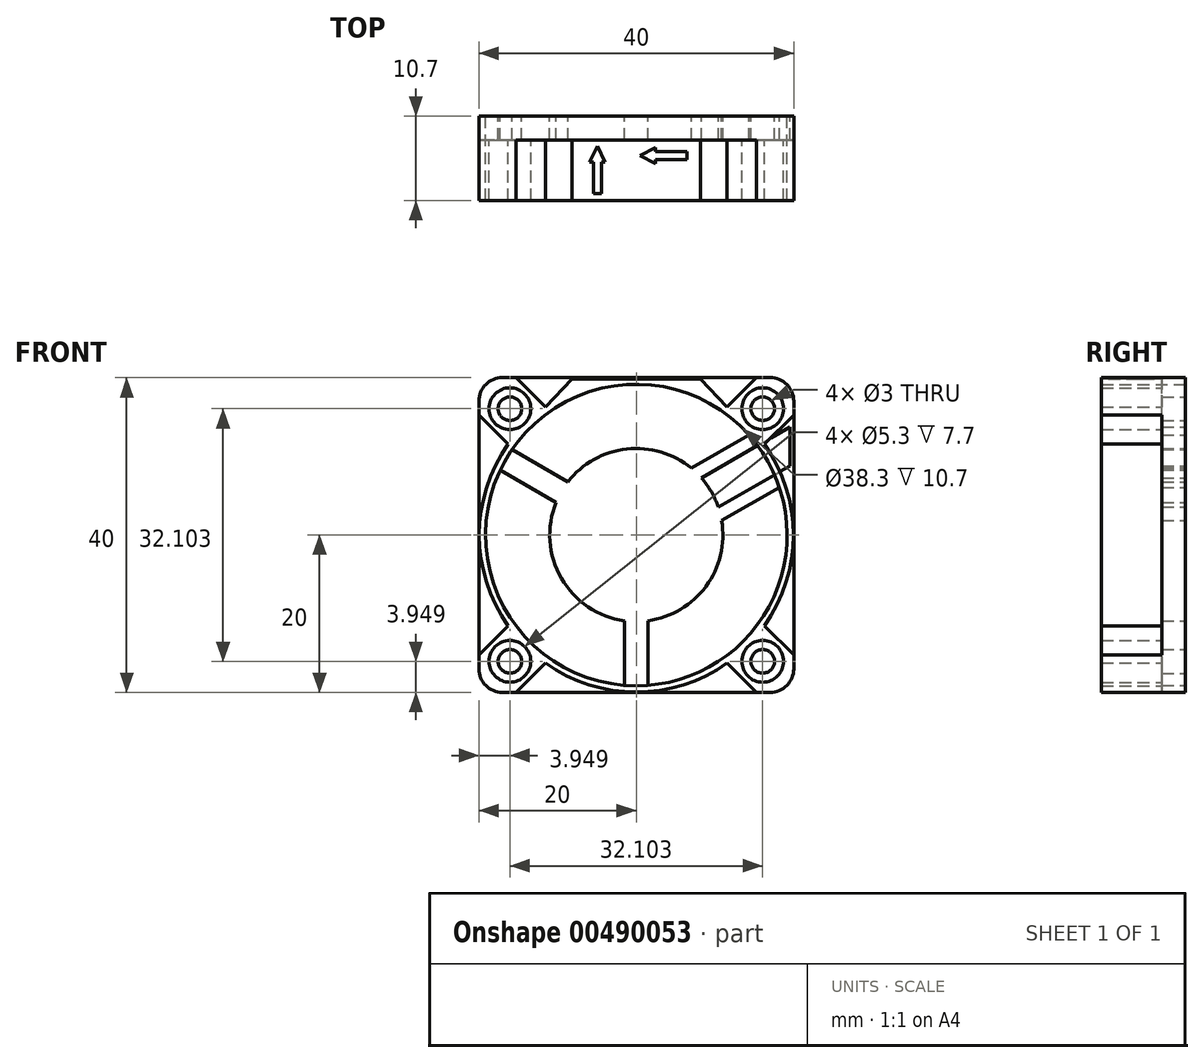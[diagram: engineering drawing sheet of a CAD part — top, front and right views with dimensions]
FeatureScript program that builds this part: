
annotation { "Feature Type Name" : "Feature", "Feature Type Description" : "" }
export const myFeature = defineFeature(function(context is Context, id is Id, definition is map)
    precondition{}
    {
        {
            var Q0;
            Q0=qCreatedBy(makeId("Front.planeOp"),FACE);
            var sketch = newSketch(context, id + "F0", { "sketchPlane" : qUnion([Q0])});
            skLineSegment(sketch, "E0.bottom", {"start": v(20, 20) * mm, "end": v(-20, 20) * mm});
            skLineSegment(sketch, "E0.top", {"start": v(20, -20) * mm, "end": v(-20, -20) * mm});
            skLineSegment(sketch, "E0.left", {"start": v(20, 20) * mm, "end": v(20, -20) * mm});
            skLineSegment(sketch, "E0.right", {"start": v(-20, 20) * mm, "end": v(-20, -20) * mm});
            skPoint(sketch, "E0.middle", {"position": v(0, 0) * mm});
            skCircle(sketch, "E1", {"center": v(0, 0) * mm, "radius": 19.15 * mm});
            skCircle(sketch, "E2", {"center": v(-16.05, 16.05) * mm, "radius": 2.65 * mm});
            skLineSegment(sketch, "E3", {"start": v(-20, 20) * mm, "end": v(0, 0) * mm, "construction": true});
            skLineSegment(sketch, "E4", {"start": v(-16.28, 11.54) * mm, "end": v(-20, 15.26) * mm});
            skCircle(sketch, "E5.0", {"center": v(0, 0) * mm, "radius": 19.95 * mm});
            skPoint(sketch, "E6", {"position": v(0, 25.11) * mm});
            skLineSegment(sketch, "E7.MirrorCS", {"start": v(-11.54, 16.28) * mm, "end": v(-15.26, 20) * mm});
            skLineSegment(sketch, "E8", {"start": v(-7.95, 20) * mm, "end": v(-11.54, 16.28) * mm});
            skCircle(sketch, "E9", {"center": v(-16.05, 16.05) * mm, "radius": 1.5 * mm});
            skLineSegment(sketch, "E10.1.0", {"start": v(-16.28, -11.54) * mm, "end": v(-20, -15.26) * mm});
            skCircle(sketch, "E10.1.1", {"center": v(-16.05, -16.05) * mm, "radius": 2.65 * mm});
            skCircle(sketch, "E10.1.2", {"center": v(-16.05, -16.05) * mm, "radius": 1.5 * mm});
            skLineSegment(sketch, "E10.1.3", {"start": v(-11.54, -16.28) * mm, "end": v(-15.26, -20) * mm});
            skLineSegment(sketch, "E10.2.0", {"start": v(11.54, -16.28) * mm, "end": v(15.26, -20) * mm});
            skCircle(sketch, "E10.2.1", {"center": v(16.05, -16.05) * mm, "radius": 2.65 * mm});
            skCircle(sketch, "E10.2.2", {"center": v(16.05, -16.05) * mm, "radius": 1.5 * mm});
            skLineSegment(sketch, "E10.2.3", {"start": v(16.28, -11.54) * mm, "end": v(20, -15.26) * mm});
            skLineSegment(sketch, "E10.3.0", {"start": v(16.28, 11.54) * mm, "end": v(20, 15.26) * mm});
            skCircle(sketch, "E10.3.1", {"center": v(16.05, 16.05) * mm, "radius": 2.65 * mm});
            skCircle(sketch, "E10.3.2", {"center": v(16.05, 16.05) * mm, "radius": 1.5 * mm});
            skLineSegment(sketch, "E10.3.3", {"start": v(11.54, 16.28) * mm, "end": v(15.26, 20) * mm});
            skLineSegment(sketch, "E11.MirrorCS", {"start": v(7.95, 20) * mm, "end": v(11.54, 16.28) * mm});
            skCircle(sketch, "E12", {"center": v(0, 0) * mm, "radius": 11 * mm});
            skLineSegment(sketch, "E13", {"start": v(-1.5, -10.9) * mm, "end": v(-1.5, -19.1) * mm});
            skLineSegment(sketch, "E14.MirrorCS", {"start": v(1.5, -10.9) * mm, "end": v(1.5, -19.1) * mm});
            skLineSegment(sketch, "E15.1.0", {"start": v(10.19, 4.15) * mm, "end": v(17.28, 8.25) * mm});
            skLineSegment(sketch, "E15.1.1", {"start": v(8.69, 6.75) * mm, "end": v(15.78, 10.84) * mm});
            skLineSegment(sketch, "E15.2.0", {"start": v(-8.69, 6.75) * mm, "end": v(-15.78, 10.84) * mm});
            skLineSegment(sketch, "E15.2.1", {"start": v(-10.19, 4.15) * mm, "end": v(-17.28, 8.25) * mm});
            skLineSegment(sketch, "E16", {"start": v(14.32, 12.71) * mm, "end": v(7, 8.49) * mm});
            skLineSegment(sketch, "E17", {"start": v(10.85, 1.82) * mm, "end": v(18.17, 6.05) * mm});
            skLineSegment(sketch, "E18", {"start": v(8.27, 7.26) * mm, "end": v(20, 14.03) * mm});
            skLineSegment(sketch, "E19", {"start": v(10.42, 3.53) * mm, "end": v(20, 9.06) * mm});
            skLineSegment(sketch, "E20", {"start": v(19.5, 13.74) * mm, "end": v(19.5, 8.78) * mm});
            skPoint(sketch, "E21", {"position": v(19.5, 11.26) * mm});
            skLineSegment(sketch, "E22.bottom", {"start": v(20, 12.76) * mm, "end": v(19.5, 12.76) * mm});
            skLineSegment(sketch, "E22.top", {"start": v(20, 9.76) * mm, "end": v(19.5, 9.76) * mm});
            skLineSegment(sketch, "E22.left", {"start": v(20, 12.76) * mm, "end": v(20, 9.76) * mm});
            skLineSegment(sketch, "E22.right", {"start": v(19.5, 12.76) * mm, "end": v(19.5, 9.76) * mm});
            skPoint(sketch, "E22.middle", {"position": v(19.75, 11.26) * mm});
            skSolve(sketch);
        }
        {
            var Q0;
            {var subQ0=sQuery(id+"F0.wireOp",EDGE,"E4");Q0=makeQuery(id+"F0.imprint","IMPRINT",FACE,{"disambiguationData":[TD([[makeQuery(id+"F0.imprint","IMPRINT",EDGE,{"derivedFrom":subQ0}),1.0]])]});}
            var Q1;
            {var subQ4=sQuery(id+"F0.wireOp",EDGE,"E1");var subQ6=makeQuery(id+"F0.imprint","INTERSECT",VERTEX,{"derivedFrom":[subQ4,sQuery(id+"F0.wireOp",EDGE,"E17")]});Q1=makeQuery(id+"F0.imprint","IMPRINT",FACE,{"disambiguationData":[TD([[makeQuery(id+"F0.imprint","IMPRINT",EDGE,{"disambiguationData":[TD([[subQ6,-1.0]])],"derivedFrom":subQ4}),-1.0]])]});}
            var Q2;
            Q2=makeQuery(id+"F0.imprint","IMPRINT",FACE,{"disambiguationData":[TD([[makeQuery(id+"F0.imprint","IMPRINT",EDGE,{"derivedFrom":sQuery(id+"F0.wireOp",EDGE,"E2")}),-1.0]])]});
            var Q3;
            {var subQ0=sQuery(id+"F0.wireOp",EDGE,"E7.MirrorCS");Q3=makeQuery(id+"F0.imprint","IMPRINT",FACE,{"disambiguationData":[TD([[makeQuery(id+"F0.imprint","IMPRINT",EDGE,{"derivedFrom":subQ0}),-1.0]])]});}
            var Q4;
            {var subQ0=sQuery(id+"F0.wireOp",EDGE,"E8");Q4=makeQuery(id+"F0.imprint","IMPRINT",FACE,{"disambiguationData":[TD([[makeQuery(id+"F0.imprint","IMPRINT",EDGE,{"derivedFrom":subQ0}),1.0]])]});}
            var Q5;
            {var subQ0=sQuery(id+"F0.wireOp",EDGE,"E10.3.3");Q5=makeQuery(id+"F0.imprint","IMPRINT",FACE,{"disambiguationData":[TD([[makeQuery(id+"F0.imprint","IMPRINT",EDGE,{"derivedFrom":subQ0}),1.0]])]});}
            var Q6;
            Q6=makeQuery(id+"F0.imprint","IMPRINT",FACE,{"disambiguationData":[TD([[makeQuery(id+"F0.imprint","IMPRINT",EDGE,{"derivedFrom":sQuery(id+"F0.wireOp",EDGE,"E10.3.1")}),-1.0]])]});
            var Q7;
            Q7=makeQuery(id+"F0.imprint","IMPRINT",FACE,{"disambiguationData":[TD([[makeQuery(id+"F0.imprint","IMPRINT",EDGE,{"derivedFrom":sQuery(id+"F0.wireOp",EDGE,"E2")}),1.0]])]});
            var Q8;
            Q8=makeQuery(id+"F0.imprint","IMPRINT",FACE,{"disambiguationData":[TD([[makeQuery(id+"F0.imprint","IMPRINT",EDGE,{"derivedFrom":sQuery(id+"F0.wireOp",EDGE,"E10.3.1")}),1.0]])]});
            var Q9;
            {var subQ0=sQuery(id+"F0.wireOp",EDGE,"E15.2.0");Q9=makeQuery(id+"F0.imprint","IMPRINT",FACE,{"disambiguationData":[TD([[makeQuery(id+"F0.imprint","IMPRINT",EDGE,{"derivedFrom":subQ0}),1.0]])]});}
            var Q10;
            {var subQ0=sQuery(id+"F0.wireOp",EDGE,"E12");var subQ5=makeQuery(id+"F0.imprint","INTERSECT",VERTEX,{"derivedFrom":[subQ0,sQuery(id+"F0.wireOp",EDGE,"E17")]});Q10=makeQuery(id+"F0.imprint","IMPRINT",FACE,{"disambiguationData":[TD([[makeQuery(id+"F0.imprint","IMPRINT",EDGE,{"disambiguationData":[TD([[subQ5,-1.0]])],"derivedFrom":subQ0}),1.0]])]});}
            var Q11;
            {var subQ0=sQuery(id+"F0.wireOp",EDGE,"E16");Q11=makeQuery(id+"F0.imprint","IMPRINT",FACE,{"disambiguationData":[TD([[makeQuery(id+"F0.imprint","IMPRINT",EDGE,{"derivedFrom":subQ0}),1.0]])]});}
            var Q12;
            {var subQ0=sQuery(id+"F0.wireOp",EDGE,"E17");Q12=makeQuery(id+"F0.imprint","IMPRINT",FACE,{"disambiguationData":[TD([[makeQuery(id+"F0.imprint","IMPRINT",EDGE,{"derivedFrom":subQ0}),1.0]])]});}
            var Q13;
            {var subQ4=sQuery(id+"F0.wireOp",EDGE,"E10.2.3");Q13=makeQuery(id+"F0.imprint","IMPRINT",FACE,{"disambiguationData":[TD([[makeQuery(id+"F0.imprint","IMPRINT",EDGE,{"derivedFrom":subQ4}),1.0]])]});}
            var Q14;
            {var subQ0=sQuery(id+"F0.wireOp",EDGE,"E10.3.0");var subQ1=sQuery(id+"F0.wireOp",EDGE,"E0.left");var subQ2=makeQuery(id+"F0.imprint","INTERSECT",VERTEX,{"derivedFrom":[subQ1,subQ0]});Q14=makeQuery(id+"F0.imprint","IMPRINT",FACE,{"disambiguationData":[TD([[makeQuery(id+"F0.imprint","IMPRINT",EDGE,{"disambiguationData":[TD([[subQ2,-1.0]])],"derivedFrom":subQ1}),-1.0]])]});}
            var Q15;
            {var subQ5=sQuery(id+"F0.wireOp",EDGE,"E20");Q15=makeQuery(id+"F0.imprint","IMPRINT",FACE,{"disambiguationData":[TD([[makeQuery(id+"F0.imprint","IMPRINT",EDGE,{"derivedFrom":subQ5}),1.0]])]});}
            var Q16;
            {var subQ0=sQuery(id+"F0.wireOp",EDGE,"E10.3.0");var subQ1=sQuery(id+"F0.wireOp",EDGE,"E5.0");var subQ2=makeQuery(id+"F0.imprint","INTERSECT",VERTEX,{"derivedFrom":[subQ1,subQ0]});Q16=makeQuery(id+"F0.imprint","IMPRINT",FACE,{"disambiguationData":[TD([[makeQuery(id+"F0.imprint","IMPRINT",EDGE,{"disambiguationData":[TD([[subQ2,-1.0]])],"derivedFrom":subQ1}),-1.0]])]});}
            var Q17;
            {var subQ0=sQuery(id+"F0.wireOp",EDGE,"E10.2.0");Q17=makeQuery(id+"F0.imprint","IMPRINT",FACE,{"disambiguationData":[TD([[makeQuery(id+"F0.imprint","IMPRINT",EDGE,{"derivedFrom":subQ0}),1.0]])]});}
            var Q18;
            {var subQ0=sQuery(id+"F0.wireOp",EDGE,"E10.1.3");Q18=makeQuery(id+"F0.imprint","IMPRINT",FACE,{"disambiguationData":[TD([[makeQuery(id+"F0.imprint","IMPRINT",EDGE,{"derivedFrom":subQ0}),1.0]])]});}
            var Q19;
            {var subQ0=sQuery(id+"F0.wireOp",EDGE,"E10.1.0");Q19=makeQuery(id+"F0.imprint","IMPRINT",FACE,{"disambiguationData":[TD([[makeQuery(id+"F0.imprint","IMPRINT",EDGE,{"derivedFrom":subQ0}),1.0]])]});}
            var Q20;
            Q20=makeQuery(id+"F0.imprint","IMPRINT",FACE,{"disambiguationData":[TD([[makeQuery(id+"F0.imprint","IMPRINT",EDGE,{"derivedFrom":sQuery(id+"F0.wireOp",EDGE,"E10.1.1")}),1.0]])]});
            var Q21;
            Q21=makeQuery(id+"F0.imprint","IMPRINT",FACE,{"disambiguationData":[TD([[makeQuery(id+"F0.imprint","IMPRINT",EDGE,{"derivedFrom":sQuery(id+"F0.wireOp",EDGE,"E10.2.1")}),1.0]])]});
            var Q22;
            {var subQ0=sQuery(id+"F0.wireOp",EDGE,"E13");Q22=makeQuery(id+"F0.imprint","IMPRINT",FACE,{"disambiguationData":[TD([[makeQuery(id+"F0.imprint","IMPRINT",EDGE,{"derivedFrom":subQ0}),1.0]])]});}
            extrude(context, id + "F1", {"entities" : qUnion([Q0, Q1, Q2, Q3, Q4, Q5, Q6, Q7, Q8, Q9, Q10, Q11, Q12, Q13, Q14, Q15, Q16, Q17, Q18, Q19, Q20, Q21, Q22]), "depth" : 3 * mm});
        }
        {
            var Q0;
            Q0=makeQuery(id+"F0.imprint","IMPRINT",FACE,{"disambiguationData":[TD([[makeQuery(id+"F0.imprint","IMPRINT",EDGE,{"derivedFrom":sQuery(id+"F0.wireOp",EDGE,"E10.3.1")}),-1.0]])]});
            var Q1;
            {var subQ0=sQuery(id+"F0.wireOp",EDGE,"E8");Q1=makeQuery(id+"F0.imprint","IMPRINT",FACE,{"disambiguationData":[TD([[makeQuery(id+"F0.imprint","IMPRINT",EDGE,{"derivedFrom":subQ0}),1.0]])]});}
            var Q2;
            Q2=makeQuery(id+"F0.imprint","IMPRINT",FACE,{"disambiguationData":[TD([[makeQuery(id+"F0.imprint","IMPRINT",EDGE,{"derivedFrom":sQuery(id+"F0.wireOp",EDGE,"E2")}),-1.0]])]});
            var Q3;
            {var subQ4=sQuery(id+"F0.wireOp",EDGE,"E1");var subQ6=makeQuery(id+"F0.imprint","INTERSECT",VERTEX,{"derivedFrom":[subQ4,sQuery(id+"F0.wireOp",EDGE,"E17")]});Q3=makeQuery(id+"F0.imprint","IMPRINT",FACE,{"disambiguationData":[TD([[makeQuery(id+"F0.imprint","IMPRINT",EDGE,{"disambiguationData":[TD([[subQ6,-1.0]])],"derivedFrom":subQ4}),-1.0]])]});}
            var Q4;
            {var subQ0=sQuery(id+"F0.wireOp",EDGE,"E1");var subQ9=makeQuery(id+"F0.imprint","INTERSECT",VERTEX,{"derivedFrom":[subQ0,sQuery(id+"F0.wireOp",EDGE,"E15.1.0")]});Q4=makeQuery(id+"F0.imprint","IMPRINT",FACE,{"disambiguationData":[TD([[makeQuery(id+"F0.imprint","IMPRINT",EDGE,{"disambiguationData":[TD([[subQ9,1.0]])],"derivedFrom":subQ0}),-1.0]])]});}
            var Q5;
            {var subQ0=sQuery(id+"F0.wireOp",EDGE,"E10.2.0");Q5=makeQuery(id+"F0.imprint","IMPRINT",FACE,{"disambiguationData":[TD([[makeQuery(id+"F0.imprint","IMPRINT",EDGE,{"derivedFrom":subQ0}),1.0]])]});}
            var Q6;
            {var subQ0=sQuery(id+"F0.wireOp",EDGE,"E10.1.0");Q6=makeQuery(id+"F0.imprint","IMPRINT",FACE,{"disambiguationData":[TD([[makeQuery(id+"F0.imprint","IMPRINT",EDGE,{"derivedFrom":subQ0}),1.0]])]});}
            var Q7;
            {var subQ0=sQuery(id+"F0.wireOp",EDGE,"E10.3.0");var subQ1=sQuery(id+"F0.wireOp",EDGE,"E5.0");var subQ2=makeQuery(id+"F0.imprint","INTERSECT",VERTEX,{"derivedFrom":[subQ1,subQ0]});Q7=makeQuery(id+"F0.imprint","IMPRINT",FACE,{"disambiguationData":[TD([[makeQuery(id+"F0.imprint","IMPRINT",EDGE,{"disambiguationData":[TD([[subQ2,-1.0]])],"derivedFrom":subQ1}),-1.0]])]});}
            extrude(context, id + "F2", {"entities" : qUnion([Q0, Q1, Q2, Q3, Q4, Q5, Q6, Q7]), "operationType" : NewBodyOperationType.ADD, "depth" : 10.7 * mm});
        }
        {
            var Q0;
            {var subQ0=sQuery(id+"F0.wireOp",EDGE,"E1");var subQ9=makeQuery(id+"F0.imprint","INTERSECT",VERTEX,{"derivedFrom":[subQ0,sQuery(id+"F0.wireOp",EDGE,"E15.1.0")]});Q0=makeQuery(id+"F0.imprint","IMPRINT",FACE,{"disambiguationData":[TD([[makeQuery(id+"F0.imprint","IMPRINT",EDGE,{"disambiguationData":[TD([[subQ9,1.0]])],"derivedFrom":subQ0}),-1.0]])]});}
            var Q1;
            {var subQ0=sQuery(id+"F0.wireOp",EDGE,"E10.3.0");var subQ1=sQuery(id+"F0.wireOp",EDGE,"E5.0");var subQ2=makeQuery(id+"F0.imprint","INTERSECT",VERTEX,{"derivedFrom":[subQ1,subQ0]});Q1=makeQuery(id+"F0.imprint","IMPRINT",FACE,{"disambiguationData":[TD([[makeQuery(id+"F0.imprint","IMPRINT",EDGE,{"disambiguationData":[TD([[subQ2,-1.0]])],"derivedFrom":subQ1}),-1.0]])]});}
            var Q2;
            {var subQ0=sQuery(id+"F0.wireOp",EDGE,"E15.2.0");var subQ1=sQuery(id+"F0.wireOp",EDGE,"E14.MirrorCS");var subQ2=sQuery(id+"F0.wireOp",EDGE,"E1");var subQ3=sQuery(id+"F0.wireOp",EDGE,"E12");var subQ4=sQuery(id+"F0.wireOp",EDGE,"E16");var subQ5=sQuery(id+"F0.wireOp",EDGE,"E13");var subQ6=sQuery(id+"F0.wireOp",EDGE,"E15.2.1");var subQ7=sQuery(id+"F0.wireOp",EDGE,"E17");var subQ8=makeQuery(id+"F0.imprint","INTERSECT",VERTEX,{"derivedFrom":[subQ3,sQuery(id+"F0.wireOp",EDGE,"E15.1.1")]});var subQ9=sQuery(id+"F0.wireOp",EDGE,"E18");var subQ10=makeQuery(id+"F0.imprint","INTERSECT",VERTEX,{"derivedFrom":[subQ3,subQ9]});var subQ11=makeQuery(id+"F0.imprint","INTERSECT",VERTEX,{"derivedFrom":[subQ3,sQuery(id+"F0.wireOp",EDGE,"E15.1.0")]});var subQ12=sQuery(id+"F0.wireOp",EDGE,"E19");var subQ13=makeQuery(id+"F0.imprint","INTERSECT",VERTEX,{"derivedFrom":[subQ2,subQ9]});var subQ14=sQuery(id+"F0.wireOp",EDGE,"E5.0");Q2=makeQuery(id+"F2.boolean.opBoolean","SPLIT",FACE,{"disambiguationData":[TD([makeQuery(id+"F1.opExtrude","SWEPT_FACE",FACE,{"disambiguationData":[OSD([subQ2]),TDD([makeQuery(id+"F0.imprint","IMPRINT",EDGE,{"disambiguationData":[TD([[makeQuery(id+"F0.imprint","INTERSECT",VERTEX,{"derivedFrom":[subQ2,subQ0]}),1.0]])],"derivedFrom":subQ2})])]}),makeQuery(id+"F1.opExtrude","SWEPT_FACE",FACE,{"disambiguationData":[OSD([subQ2]),TDD([makeQuery(id+"F0.imprint","IMPRINT",EDGE,{"disambiguationData":[TD([[makeQuery(id+"F0.imprint","INTERSECT",VERTEX,{"derivedFrom":[subQ2,subQ5]}),1.0]])],"derivedFrom":subQ2})])]}),makeQuery(id+"F1.opExtrude","SWEPT_FACE",FACE,{"disambiguationData":[OSD([subQ2]),TDD([makeQuery(id+"F0.imprint","IMPRINT",EDGE,{"disambiguationData":[TD([[makeQuery(id+"F0.imprint","INTERSECT",VERTEX,{"derivedFrom":[subQ2,subQ1]}),-1.0]])],"derivedFrom":subQ2})])]}),makeQuery(id+"F1.opExtrude","SWEPT_FACE",FACE,{"disambiguationData":[OSD([subQ3]),TDD([makeQuery(id+"F0.imprint","IMPRINT",EDGE,{"disambiguationData":[TD([[subQ11,1.0]])],"derivedFrom":subQ3}),makeQuery(id+"F0.imprint","IMPRINT",EDGE,{"disambiguationData":[TD([[subQ11,-1.0]])],"derivedFrom":subQ3}),makeQuery(id+"F0.imprint","IMPRINT",EDGE,{"disambiguationData":[TD([[subQ8,-1.0]])],"derivedFrom":subQ3})])]}),makeQuery(id+"F1.opExtrude","SWEPT_FACE",FACE,{"disambiguationData":[OSD([subQ3]),TDD([makeQuery(id+"F0.imprint","IMPRINT",EDGE,{"disambiguationData":[TD([[makeQuery(id+"F0.imprint","INTERSECT",VERTEX,{"derivedFrom":[subQ3,subQ0]}),1.0]])],"derivedFrom":subQ3})])]}),makeQuery(id+"F1.opExtrude","SWEPT_FACE",FACE,{"disambiguationData":[OSD([subQ3]),TDD([makeQuery(id+"F0.imprint","IMPRINT",EDGE,{"disambiguationData":[TD([[makeQuery(id+"F0.imprint","INTERSECT",VERTEX,{"derivedFrom":[subQ3,subQ5]}),1.0]])],"derivedFrom":subQ3})])]}),makeQuery(id+"F1.opExtrude","SWEPT_FACE",FACE,{"disambiguationData":[OSD([subQ3]),TDD([makeQuery(id+"F0.imprint","IMPRINT",EDGE,{"disambiguationData":[TD([[makeQuery(id+"F0.imprint","INTERSECT",VERTEX,{"derivedFrom":[subQ3,subQ1]}),-1.0]])],"derivedFrom":subQ3})])]}),makeQuery(id+"F1.opExtrude","SWEPT_FACE",FACE,{"disambiguationData":[OSD([subQ5])]}),makeQuery(id+"F1.opExtrude","SWEPT_FACE",FACE,{"disambiguationData":[OSD([subQ1])]}),makeQuery(id+"F1.opExtrude","SWEPT_FACE",FACE,{"disambiguationData":[OSD([subQ0])]}),makeQuery(id+"F1.opExtrude","SWEPT_FACE",FACE,{"disambiguationData":[OSD([subQ6])]}),makeQuery(id+"F1.opExtrude","SWEPT_FACE",FACE,{"disambiguationData":[OSD([subQ4])]}),makeQuery(id+"F1.opExtrude","SWEPT_FACE",FACE,{"disambiguationData":[OSD([subQ7])]}),makeQuery(id+"F1.opExtrude","SWEPT_FACE",FACE,{"disambiguationData":[OSD([subQ9]),TDD([makeQuery(id+"F0.imprint","IMPRINT",EDGE,{"disambiguationData":[TD([[subQ10,-1.0]])],"derivedFrom":subQ9}),makeQuery(id+"F0.imprint","IMPRINT",EDGE,{"disambiguationData":[TD([[subQ13,-1.0]])],"derivedFrom":subQ9})])]}),makeQuery(id+"F1.opExtrude","SWEPT_FACE",FACE,{"disambiguationData":[OSD([subQ12])]}),makeQuery(id+"F2.opExtrude","SWEPT_FACE",FACE,{"disambiguationData":[OSD([subQ2])]})])],"derivedFrom":makeQuery(id+"F1.opExtrude","CAP_FACE",FACE,{"disambiguationData":[OSD([sQuery(id+"F0.wireOp",EDGE,"E0.bottom"),sQuery(id+"F0.wireOp",EDGE,"E0.top"),sQuery(id+"F0.wireOp",EDGE,"E0.left"),sQuery(id+"F0.wireOp",EDGE,"E0.right"),subQ2,subQ14,sQuery(id+"F0.wireOp",EDGE,"E9"),sQuery(id+"F0.wireOp",EDGE,"E10.1.2"),sQuery(id+"F0.wireOp",EDGE,"E10.2.2"),sQuery(id+"F0.wireOp",EDGE,"E10.3.0"),sQuery(id+"F0.wireOp",EDGE,"E10.3.2"),subQ3,subQ5,subQ1,subQ0,subQ6,subQ4,subQ7,subQ9,subQ12,sQuery(id+"F0.wireOp",EDGE,"E20")])],"isStart":false})});}
            var Q3;
            Q3=makeQuery(id+"F1.opExtrude","CAP_VERTEX",VERTEX,{"disambiguationData":[OSD([sQuery(id+"F0.wireOp",EDGE,"E10.3.0"),sQuery(id+"F0.wireOp",EDGE,"E18")])],"isStart":false});
            extrude(context, id + "F3", {"entities" : qUnion([Q0, Q1]), "operationType" : NewBodyOperationType.REMOVE, "endBound" : BoundingType.UP_TO_VERTEX, "endBoundEntityFace" : qUnion([Q2]), "endBoundEntityVertex" : qUnion([Q3]), "depth" : 25 * mm});
        }
        {
            var Q0;
            {var subQ0=sQuery(id+"F0.wireOp",EDGE,"E0.right");var subQ1=sQuery(id+"F0.wireOp",EDGE,"E0.top");Q0=makeQuery(id+"F2.boolean.opBoolean","MERGE",EDGE,{"derivedFrom":[makeQuery(id+"F1.opExtrude","SWEPT_EDGE",EDGE,{"disambiguationData":[OSD([subQ1,subQ0])]}),makeQuery(id+"F2.opExtrude","SWEPT_EDGE",EDGE,{"disambiguationData":[OSD([subQ1,subQ0])]})]});}
            var Q1;
            {var subQ0=sQuery(id+"F0.wireOp",EDGE,"E0.left");var subQ1=sQuery(id+"F0.wireOp",EDGE,"E0.top");Q1=makeQuery(id+"F2.boolean.opBoolean","MERGE",EDGE,{"derivedFrom":[makeQuery(id+"F1.opExtrude","SWEPT_EDGE",EDGE,{"disambiguationData":[OSD([subQ1,subQ0])]}),makeQuery(id+"F2.opExtrude","SWEPT_EDGE",EDGE,{"disambiguationData":[OSD([subQ1,subQ0])]})]});}
            var Q2;
            {var subQ0=sQuery(id+"F0.wireOp",EDGE,"E0.left");var subQ1=sQuery(id+"F0.wireOp",EDGE,"E0.bottom");Q2=makeQuery(id+"F2.boolean.opBoolean","MERGE",EDGE,{"derivedFrom":[makeQuery(id+"F1.opExtrude","SWEPT_EDGE",EDGE,{"disambiguationData":[OSD([subQ1,subQ0])]}),makeQuery(id+"F2.opExtrude","SWEPT_EDGE",EDGE,{"disambiguationData":[OSD([subQ1,subQ0])]})]});}
            var Q3;
            {var subQ0=sQuery(id+"F0.wireOp",EDGE,"E0.right");var subQ1=sQuery(id+"F0.wireOp",EDGE,"E0.bottom");Q3=makeQuery(id+"F2.boolean.opBoolean","MERGE",EDGE,{"derivedFrom":[makeQuery(id+"F1.opExtrude","SWEPT_EDGE",EDGE,{"disambiguationData":[OSD([subQ1,subQ0])]}),makeQuery(id+"F2.opExtrude","SWEPT_EDGE",EDGE,{"disambiguationData":[OSD([subQ1,subQ0])]})]});}
            fillet(context, id + "F4", {"entities" : qUnion([Q0, Q1, Q2, Q3]), "radius" : 3 * mm, "tangentPropagation" : true, "allowEdgeOverflow" : false});
        }
        {
            var Q0;
            {var subQ0=sQuery(id+"F0.wireOp",EDGE,"E0.bottom");Q0=makeQuery(id+"F2.boolean.opBoolean","MERGE",FACE,{"derivedFrom":[makeQuery(id+"F1.opExtrude","SWEPT_FACE",FACE,{"disambiguationData":[OSD([subQ0])]}),makeQuery(id+"F2.opExtrude","SWEPT_FACE",FACE,{"disambiguationData":[OSD([subQ0]),TDD([makeQuery(id+"F0.imprint","IMPRINT",EDGE,{"disambiguationData":[TD([[makeQuery(id+"F0.imprint","INTERSECT",VERTEX,{"derivedFrom":[subQ0,sQuery(id+"F0.wireOp",EDGE,"E0.left")]}),-1.0]])],"derivedFrom":subQ0})])]}),makeQuery(id+"F2.opExtrude","SWEPT_FACE",FACE,{"disambiguationData":[OSD([subQ0]),TDD([makeQuery(id+"F0.imprint","IMPRINT",EDGE,{"disambiguationData":[TD([[makeQuery(id+"F0.imprint","INTERSECT",VERTEX,{"derivedFrom":[subQ0,sQuery(id+"F0.wireOp",EDGE,"E8")]}),1.0]])],"derivedFrom":subQ0})])]}),makeQuery(id+"F2.opExtrude","SWEPT_FACE",FACE,{"disambiguationData":[OSD([subQ0]),TDD([makeQuery(id+"F0.imprint","IMPRINT",EDGE,{"disambiguationData":[TD([[makeQuery(id+"F0.imprint","INTERSECT",VERTEX,{"derivedFrom":[subQ0,sQuery(id+"F0.wireOp",EDGE,"E0.right")]}),1.0]])],"derivedFrom":subQ0})])]})]});}
            var sketch = newSketch(context, id + "F5", { "sketchPlane" : qUnion([Q0])});
            skLineSegment(sketch, "E23.bottom", {"start": v(6.45, -5.5) * mm, "end": v(2.45, -5.5) * mm});
            skLineSegment(sketch, "E23.top", {"start": v(6.45, -4.5) * mm, "end": v(2.45, -4.5) * mm});
            skLineSegment(sketch, "E23.left", {"start": v(6.45, -5.5) * mm, "end": v(6.45, -4.5) * mm});
            skLineSegment(sketch, "E23.right", {"start": v(2.45, -5.5) * mm, "end": v(2.45, -4.5) * mm});
            skPoint(sketch, "E23.middle", {"position": v(4.45, -5) * mm});
            skLineSegment(sketch, "E24", {"start": v(2.45, -4) * mm, "end": v(2.45, -6) * mm});
            skLineSegment(sketch, "E25", {"start": v(2.45, -6) * mm, "end": v(0.45, -5) * mm});
            skLineSegment(sketch, "E26", {"start": v(0.45, -5) * mm, "end": v(2.45, -4) * mm});
            skPoint(sketch, "E27", {"position": v(2.45, -5) * mm});
            skLineSegment(sketch, "E28.bottom", {"start": v(-5.45, -9.8) * mm, "end": v(-5.45, -5.8) * mm});
            skLineSegment(sketch, "E28.top", {"start": v(-4.45, -9.8) * mm, "end": v(-4.45, -5.8) * mm});
            skLineSegment(sketch, "E28.left", {"start": v(-5.45, -9.8) * mm, "end": v(-4.45, -9.8) * mm});
            skLineSegment(sketch, "E28.right", {"start": v(-5.45, -5.8) * mm, "end": v(-4.45, -5.8) * mm});
            skPoint(sketch, "E28.middle", {"position": v(-4.95, -7.8) * mm});
            skLineSegment(sketch, "E29", {"start": v(-3.95, -5.8) * mm, "end": v(-5.95, -5.8) * mm});
            skLineSegment(sketch, "E30", {"start": v(-5.95, -5.8) * mm, "end": v(-4.95, -3.8) * mm});
            skLineSegment(sketch, "E31", {"start": v(-4.95, -3.8) * mm, "end": v(-3.95, -5.8) * mm});
            skPoint(sketch, "E32", {"position": v(-4.95, -5.8) * mm});
            skLineSegment(sketch, "E33.bottom", {"start": v(-9.95, -3) * mm, "end": v(9.95, -3) * mm});
            skLineSegment(sketch, "E33.top", {"start": v(-9.95, -10.7) * mm, "end": v(9.95, -10.7) * mm});
            skLineSegment(sketch, "E33.left", {"start": v(-9.95, -3) * mm, "end": v(-9.95, -10.7) * mm});
            skLineSegment(sketch, "E33.right", {"start": v(9.95, -3) * mm, "end": v(9.95, -10.7) * mm});
            skSolve(sketch);
        }
        {
            var Q0;
            {var subQ4=sQuery(id+"F5.wireOp",EDGE,"E33.left");Q0=makeQuery(id+"F5.imprint","IMPRINT",FACE,{"disambiguationData":[TD([[makeQuery(id+"F5.imprint","IMPRINT",EDGE,{"derivedFrom":subQ4}),1.0]])]});}
            var Q1;
            {var subQ5=sQuery(id+"F5.wireOp",EDGE,"E23.bottom");Q1=makeQuery(id+"F5.imprint","IMPRINT",FACE,{"disambiguationData":[TD([[makeQuery(id+"F5.imprint","IMPRINT",EDGE,{"derivedFrom":subQ5}),1.0]])]});}
            var Q2;
            {var subQ4=sQuery(id+"F5.wireOp",EDGE,"E33.right");Q2=makeQuery(id+"F5.imprint","IMPRINT",FACE,{"disambiguationData":[TD([[makeQuery(id+"F5.imprint","IMPRINT",EDGE,{"derivedFrom":subQ4}),-1.0]])]});}
            extrude(context, id + "F6", {"entities" : qUnion([Q0, Q1, Q2]), "operationType" : NewBodyOperationType.REMOVE, "oppositeDirection" : true, "depth" : 0.2 * mm});
        }
    });
